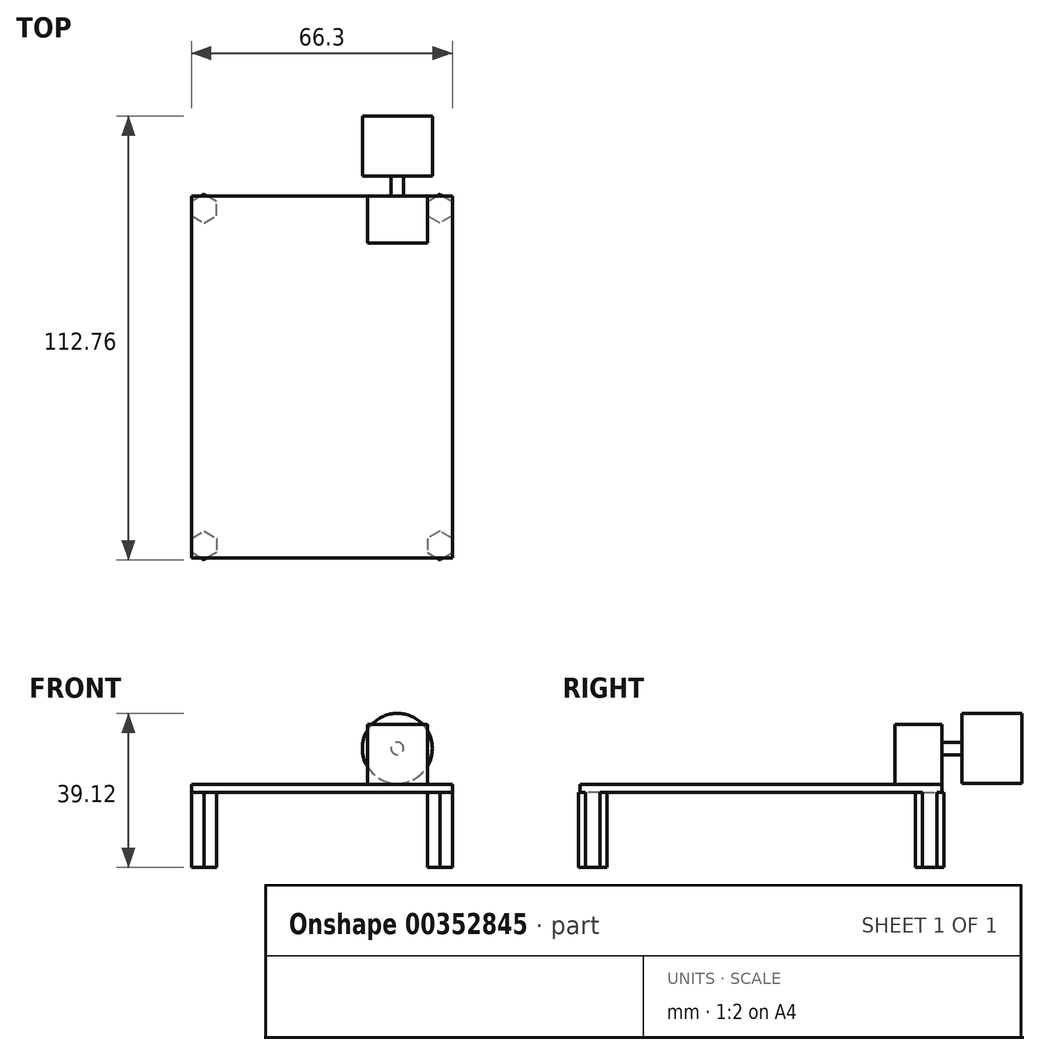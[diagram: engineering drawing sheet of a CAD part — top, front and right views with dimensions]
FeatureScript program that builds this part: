
annotation { "Feature Type Name" : "Feature", "Feature Type Description" : "" }
export const myFeature = defineFeature(function(context is Context, id is Id, definition is map)
    precondition{}
    {
        {
            var Q0;
            Q0=qCreatedBy(makeId("Top.planeOp"),FACE);
            var sketch = newSketch(context, id + "F0", { "sketchPlane" : qUnion([Q0])});
            skLineSegment(sketch, "E0.bottom", {"start": v(33.15, 45.97) * mm, "end": v(-33.15, 45.97) * mm});
            skLineSegment(sketch, "E0.top", {"start": v(33.15, -45.97) * mm, "end": v(-33.15, -45.97) * mm});
            skLineSegment(sketch, "E0.left", {"start": v(33.15, 45.97) * mm, "end": v(33.15, -45.97) * mm});
            skLineSegment(sketch, "E0.right", {"start": v(-33.15, 45.97) * mm, "end": v(-33.15, -45.97) * mm});
            skPoint(sketch, "E0.middle", {"position": v(0, 0) * mm});
            skSolve(sketch);
        }
        {
            var Q0;
            Q0 = qSketchRegion(id + "F0", true);
            extrude(context, id + "F1", {"entities" : qUnion([Q0]), "depth" : 2.03 * mm});
        }
        {
            var Q0;
            Q0=makeQuery(id+"F1.opExtrude","CAP_FACE",FACE,{"disambiguationData":[OSD([sQuery(id+"F0.wireOp",EDGE,"E0.bottom"),sQuery(id+"F0.wireOp",EDGE,"E0.top"),sQuery(id+"F0.wireOp",EDGE,"E0.left"),sQuery(id+"F0.wireOp",EDGE,"E0.right")])],"isStart":false});
            var sketch = newSketch(context, id + "F2", { "sketchPlane" : qUnion([Q0])});
            skLineSegment(sketch, "E1.bottom", {"start": v(11.56, 45.97) * mm, "end": v(26.8, 45.97) * mm});
            skLineSegment(sketch, "E1.top", {"start": v(11.56, 34.04) * mm, "end": v(26.8, 34.04) * mm});
            skLineSegment(sketch, "E1.left", {"start": v(11.56, 45.97) * mm, "end": v(11.56, 34.04) * mm});
            skLineSegment(sketch, "E1.right", {"start": v(26.8, 45.97) * mm, "end": v(26.8, 34.04) * mm});
            skSolve(sketch);
        }
        {
            var Q0;
            Q0 = qSketchRegion(id + "F2", true);
            extrude(context, id + "F3", {"entities" : qUnion([Q0]), "operationType" : NewBodyOperationType.ADD, "depth" : 15.24 * mm});
        }
        {
            var Q0;
            Q0=makeQuery(id+"F3.boolean.opBoolean","MERGE",FACE,{"derivedFrom":[makeQuery(id+"F1.opExtrude","SWEPT_FACE",FACE,{"disambiguationData":[OSD([sQuery(id+"F0.wireOp",EDGE,"E0.bottom")])]}),makeQuery(id+"F3.opExtrude","SWEPT_FACE",FACE,{"disambiguationData":[OSD([sQuery(id+"F2.wireOp",EDGE,"E1.bottom")])]})]});
            var sketch = newSketch(context, id + "F4", { "sketchPlane" : qUnion([Q0])});
            skCircle(sketch, "E2", {"center": v(-19.18, 11.18) * mm, "radius": 1.59 * mm});
            skPoint(sketch, "E2.centerSnap0", {"position": v(-19.18, 17.27) * mm});
            skSolve(sketch);
        }
        {
            var Q0;
            Q0 = qSketchRegion(id + "F4", true);
            extrude(context, id + "F5", {"entities" : qUnion([Q0]), "operationType" : NewBodyOperationType.ADD, "depth" : 20.32 * mm});
        }
        {
            var Q0;
            Q0=makeQuery(id+"F5.opExtrude","CAP_FACE",FACE,{"disambiguationData":[OSD([sQuery(id+"F4.wireOp",EDGE,"E2")])],"isStart":false});
            var sketch = newSketch(context, id + "F6", { "sketchPlane" : qUnion([Q0])});
            skCircle(sketch, "E3", {"center": v(-19.18, 11.18) * mm, "radius": 8.9 * mm});
            skSolve(sketch);
        }
        {
            var Q0;
            Q0 = qSketchRegion(id + "F6", true);
            extrude(context, id + "F7", {"entities" : qUnion([Q0]), "operationType" : NewBodyOperationType.ADD, "oppositeDirection" : true, "depth" : 15.24 * mm});
        }
        {
            var Q0;
            Q0=makeQuery(id+"F1.opExtrude","CAP_FACE",FACE,{"disambiguationData":[OSD([sQuery(id+"F0.wireOp",EDGE,"E0.bottom"),sQuery(id+"F0.wireOp",EDGE,"E0.top"),sQuery(id+"F0.wireOp",EDGE,"E0.left"),sQuery(id+"F0.wireOp",EDGE,"E0.right")])],"isStart":true});
            var sketch = newSketch(context, id + "F8", { "sketchPlane" : qUnion([Q0])});
            skCircle(sketch, "E4.cCircle", {"center": v(29.97, 42.8) * mm, "radius": 3.18 * mm, "construction": true});
            skLineSegment(sketch, "E4.0", {"start": v(33.15, 44.63) * mm, "end": v(33.15, 40.97) * mm});
            skLineSegment(sketch, "E4.1", {"start": v(33.15, 40.97) * mm, "end": v(29.97, 39.13) * mm});
            skLineSegment(sketch, "E4.2", {"start": v(29.97, 39.13) * mm, "end": v(26.8, 40.97) * mm});
            skLineSegment(sketch, "E4.3", {"start": v(26.8, 40.97) * mm, "end": v(26.8, 44.63) * mm});
            skLineSegment(sketch, "E4.4", {"start": v(26.8, 44.63) * mm, "end": v(29.97, 46.47) * mm});
            skLineSegment(sketch, "E4.5", {"start": v(29.97, 46.47) * mm, "end": v(33.15, 44.63) * mm});
            skPoint(sketch, "E4.0.midPoint", {"position": v(33.15, 42.8) * mm});
            skLineSegment(sketch, "E5.MirrorCS", {"start": v(-33.15, 44.63) * mm, "end": v(-33.15, 40.97) * mm});
            skPoint(sketch, "E6.MirrorP", {"position": v(-33.15, 42.8) * mm});
            skCircle(sketch, "E7.MirrorC", {"center": v(-29.97, 42.8) * mm, "radius": 3.18 * mm, "construction": true});
            skLineSegment(sketch, "E8.MirrorCS", {"start": v(-33.15, 40.97) * mm, "end": v(-29.97, 39.13) * mm});
            skLineSegment(sketch, "E9.MirrorCS", {"start": v(-29.97, 39.13) * mm, "end": v(-26.8, 40.97) * mm});
            skLineSegment(sketch, "E10.MirrorCS", {"start": v(-26.8, 40.97) * mm, "end": v(-26.8, 44.63) * mm});
            skLineSegment(sketch, "E11.MirrorCS", {"start": v(-26.8, 44.63) * mm, "end": v(-29.97, 46.47) * mm});
            skLineSegment(sketch, "E12.MirrorCS", {"start": v(-29.97, 46.47) * mm, "end": v(-33.15, 44.63) * mm});
            skLineSegment(sketch, "E13.MirrorCS", {"start": v(29.97, -46.47) * mm, "end": v(33.15, -44.63) * mm});
            skLineSegment(sketch, "E14.MirrorCS", {"start": v(26.8, -44.63) * mm, "end": v(29.97, -46.47) * mm});
            skLineSegment(sketch, "E15.MirrorCS", {"start": v(33.15, -44.63) * mm, "end": v(33.15, -40.97) * mm});
            skLineSegment(sketch, "E16.MirrorCS", {"start": v(-33.15, -44.63) * mm, "end": v(-33.15, -40.97) * mm});
            skLineSegment(sketch, "E17.MirrorCS", {"start": v(-33.15, -40.97) * mm, "end": v(-29.97, -39.13) * mm});
            skLineSegment(sketch, "E18.MirrorCS", {"start": v(-26.8, -44.63) * mm, "end": v(-29.97, -46.47) * mm});
            skPoint(sketch, "E19.MirrorP", {"position": v(-33.15, -42.8) * mm});
            skPoint(sketch, "E20.MirrorP", {"position": v(33.15, -42.8) * mm});
            skLineSegment(sketch, "E21.MirrorCS", {"start": v(26.8, -40.97) * mm, "end": v(26.8, -44.63) * mm});
            skLineSegment(sketch, "E22.MirrorCS", {"start": v(29.97, -39.13) * mm, "end": v(26.8, -40.97) * mm});
            skLineSegment(sketch, "E23.MirrorCS", {"start": v(33.15, -40.97) * mm, "end": v(29.97, -39.13) * mm});
            skCircle(sketch, "E24.MirrorC", {"center": v(29.97, -42.8) * mm, "radius": 3.18 * mm, "construction": true});
            skLineSegment(sketch, "E25.MirrorCS", {"start": v(-29.97, -46.47) * mm, "end": v(-33.15, -44.63) * mm});
            skCircle(sketch, "E26.MirrorC", {"center": v(-29.97, -42.8) * mm, "radius": 3.18 * mm, "construction": true});
            skLineSegment(sketch, "E27.MirrorCS", {"start": v(-29.97, -39.13) * mm, "end": v(-26.8, -40.97) * mm});
            skLineSegment(sketch, "E28.MirrorCS", {"start": v(-26.8, -40.97) * mm, "end": v(-26.8, -44.63) * mm});
            skSolve(sketch);
        }
        {
            var Q0;
            Q0 = qSketchRegion(id + "F8", true);
            extrude(context, id + "F9", {"entities" : qUnion([Q0]), "operationType" : NewBodyOperationType.ADD, "depth" : 19.05 * mm});
        }
    });
